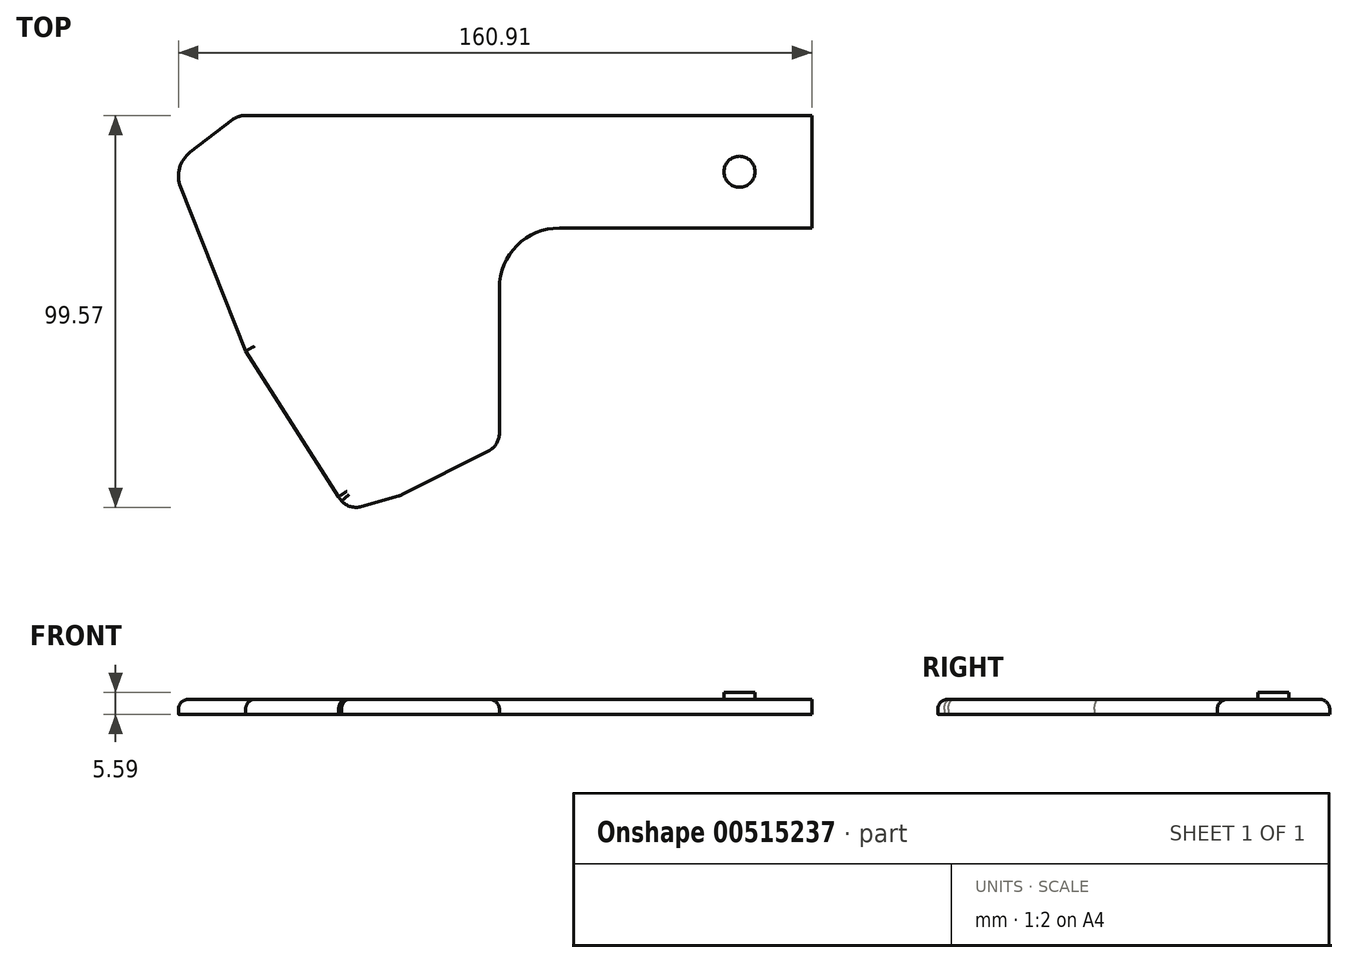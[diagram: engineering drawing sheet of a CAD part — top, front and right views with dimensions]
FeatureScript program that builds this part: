
annotation { "Feature Type Name" : "Feature", "Feature Type Description" : "" }
export const myFeature = defineFeature(function(context is Context, id is Id, definition is map)
    precondition{}
    {
        {
            var Q0;
            Q0=qCreatedBy(makeId("Top.planeOp"),FACE);
            var sketch = newSketch(context, id + "F0", { "sketchPlane" : qUnion([Q0])});
            skLineSegment(sketch, "E0.0", {"start": v(-43.43, -337.67) * mm, "end": v(-15.96, -337.67) * mm});
            skLineSegment(sketch, "E1.0", {"start": v(-160.03, -337.67) * mm, "end": v(-44.7, -337.67) * mm});
            skLineSegment(sketch, "E2.0", {"start": v(-43.43, -309.1) * mm, "end": v(-15.96, -309.1) * mm});
            skLineSegment(sketch, "E3.0", {"start": v(-80.1, -309.1) * mm, "end": v(-44.7, -309.1) * mm});
            skArc(sketch, "E4.0", {"start": v(-80.1, -309.1) * mm, "mid": v(-90.87, -304.63) * mm, "end": v(-95.34, -293.85) * mm});
            skLineSegment(sketch, "E5.0", {"start": v(-95.34, -293.85) * mm, "end": v(-95.34, -256.97) * mm});
            skArc(sketch, "E6.0", {"start": v(-95.34, -256.97) * mm, "mid": v(-96.09, -254.3) * mm, "end": v(-98.12, -252.43) * mm});
            skLineSegment(sketch, "E7.0", {"start": v(-98.12, -252.43) * mm, "end": v(-120.03, -241.33) * mm});
            skArc(sketch, "E8.0", {"start": v(-120.03, -241.33) * mm, "mid": v(-120.47, -241.13) * mm, "end": v(-120.93, -240.97) * mm});
            skLineSegment(sketch, "E9.0", {"start": v(-130.32, -238.3) * mm, "end": v(-120.93, -240.97) * mm});
            skArc(sketch, "E10.0", {"start": v(-130.32, -238.3) * mm, "mid": v(-133.1, -238.29) * mm, "end": v(-135.45, -239.74) * mm});
            skLineSegment(sketch, "E11.0", {"start": v(-136.2, -240.77) * mm, "end": v(-141.2, -248.63) * mm});
            skLineSegment(sketch, "E12.0", {"start": v(-151.3, -264.49) * mm, "end": v(-159.82, -277.9) * mm});
            skLineSegment(sketch, "E13.0", {"start": v(-159.82, -277.9) * mm, "end": v(-165.67, -292.62) * mm});
            skLineSegment(sketch, "E14.0", {"start": v(-172.6, -310.09) * mm, "end": v(-176.33, -319.47) * mm});
            skArc(sketch, "E15.0", {"start": v(-176.33, -319.47) * mm, "mid": v(-176.6, -324.3) * mm, "end": v(-173.9, -328.33) * mm});
            skPoint(sketch, "E16.0", {"position": v(-168.51, -332.47) * mm});
            skLineSegment(sketch, "E17.0", {"start": v(-173.9, -328.33) * mm, "end": v(-163.13, -336.61) * mm});
            skArc(sketch, "E18.0", {"start": v(-163.13, -336.61) * mm, "mid": v(-161.67, -337.4) * mm, "end": v(-160.03, -337.67) * mm});
            skLineSegment(sketch, "E19", {"start": v(-172.6, -310.09) * mm, "end": v(-165.67, -292.62) * mm});
            skLineSegment(sketch, "E20", {"start": v(-151.3, -264.49) * mm, "end": v(-141.2, -248.63) * mm});
            skLineSegment(sketch, "E21", {"start": v(-136.2, -240.77) * mm, "end": v(-135.45, -239.74) * mm});
            skLineSegment(sketch, "E22", {"start": v(-44.7, -309.1) * mm, "end": v(-43.43, -309.1) * mm});
            skLineSegment(sketch, "E23", {"start": v(-44.7, -337.67) * mm, "end": v(-43.43, -337.67) * mm});
            skLineSegment(sketch, "E24", {"start": v(-15.96, -337.67) * mm, "end": v(-15.96, -309.1) * mm});
            skSolve(sketch);
        }
        {
            var Q0;
            Q0=makeQuery(id+"F0.imprint","IMPRINT",FACE,{"disambiguationData":[TD([[makeQuery(id+"F0.imprint","IMPRINT",EDGE,{"derivedFrom":sQuery(id+"F0.wireOp",EDGE,"d1444f51-8acc-4532-b601-094db481933f.0")}),-1.0]])]});
            var Q1;
            Q1=makeQuery(id+"F0.imprint","IMPRINT",FACE,{"disambiguationData":[TD([[makeQuery(id+"F0.imprint","IMPRINT",EDGE,{"derivedFrom":sQuery(id+"F0.wireOp",EDGE,"E0.0")}),1.0]])]});
            var Q2;
            Q2=qConstructionFilter(qBodyType(qCreatedBy(id+"F0",EDGE),BodyType.WIRE),ConstructionObject.NO);
            extrude(context, id + "F1", {"entities" : qUnion([Q0, Q1]), "surfaceEntities" : qUnion([Q2]), "depth" : 3.81 * mm});
        }
        {
            var Q0;
            Q0=makeQuery(id+"F1.opExtrude","CAP_EDGE",EDGE,{"disambiguationData":[OSD([sQuery(id+"F0.wireOp",EDGE,"E21")])],"isStart":false});
            var Q1;
            Q1=makeQuery(id+"F1.opExtrude","CAP_EDGE",EDGE,{"disambiguationData":[OSD([sQuery(id+"F0.wireOp",EDGE,"E9.0")])],"isStart":false});
            var Q2;
            Q2=makeQuery(id+"F1.opExtrude","CAP_EDGE",EDGE,{"disambiguationData":[OSD([sQuery(id+"F0.wireOp",EDGE,"E0.0"),sQuery(id+"F0.wireOp",EDGE,"E1.0"),sQuery(id+"F0.wireOp",EDGE,"E23")])],"isStart":false});
            fillet(context, id + "F2", {"entities" : qUnion([Q0, Q1, Q2]), "radius" : 2.54 * mm, "tangentPropagation" : true, "allowEdgeOverflow" : false});
        }
        {
            var Q0;
            Q0=makeQuery(id+"F1.opExtrude","CAP_FACE",FACE,{"disambiguationData":[OSD([sQuery(id+"F0.wireOp",EDGE,"E0.0"),sQuery(id+"F0.wireOp",EDGE,"E1.0"),sQuery(id+"F0.wireOp",EDGE,"E2.0"),sQuery(id+"F0.wireOp",EDGE,"E3.0"),sQuery(id+"F0.wireOp",EDGE,"E4.0"),sQuery(id+"F0.wireOp",EDGE,"E5.0"),sQuery(id+"F0.wireOp",EDGE,"E6.0"),sQuery(id+"F0.wireOp",EDGE,"E7.0"),sQuery(id+"F0.wireOp",EDGE,"E8.0"),sQuery(id+"F0.wireOp",EDGE,"E9.0"),sQuery(id+"F0.wireOp",EDGE,"E10.0"),sQuery(id+"F0.wireOp",EDGE,"E11.0"),sQuery(id+"F0.wireOp",EDGE,"E12.0"),sQuery(id+"F0.wireOp",EDGE,"E13.0"),sQuery(id+"F0.wireOp",EDGE,"E14.0"),sQuery(id+"F0.wireOp",EDGE,"E15.0"),sQuery(id+"F0.wireOp",EDGE,"E17.0"),sQuery(id+"F0.wireOp",EDGE,"E18.0"),sQuery(id+"F0.wireOp",EDGE,"E19"),sQuery(id+"F0.wireOp",EDGE,"E20"),sQuery(id+"F0.wireOp",EDGE,"E21"),sQuery(id+"F0.wireOp",EDGE,"E22"),sQuery(id+"F0.wireOp",EDGE,"E23"),sQuery(id+"F0.wireOp",EDGE,"E24")])],"isStart":false});
            var sketch = newSketch(context, id + "F3", { "sketchPlane" : qUnion([Q0])});
            skCircle(sketch, "E25.0", {"center": v(-34.35, -323.38) * mm, "radius": 3.94 * mm});
            skLineSegment(sketch, "E26", {"start": v(-97.88, -323.38) * mm, "end": v(-34.35, -323.38) * mm});
            skLineSegment(sketch, "E27", {"start": v(-97.88, -293.85) * mm, "end": v(-97.88, -335.13) * mm});
            skLineSegment(sketch, "E28", {"start": v(-34.35, -323.38) * mm, "end": v(-34.35, -311.63) * mm});
            skLineSegment(sketch, "E29", {"start": v(-34.35, -323.38) * mm, "end": v(-34.35, -335.13) * mm});
            skSolve(sketch);
        }
        {
            var Q0;
            Q0=qSketchRegion(id+"F3",true);
            extrude(context, id + "F4", {"entities" : qUnion([Q0]), "operationType" : NewBodyOperationType.ADD, "depth" : 1.78 * mm});
        }
        {
            var Q0;
            Q0=makeQuery(id+"F1.opExtrude","SWEPT_BODY",BODY,{"disambiguationData":[OSD([sQuery(id+"F0.wireOp",EDGE,"E0.0"),sQuery(id+"F0.wireOp",EDGE,"E1.0"),sQuery(id+"F0.wireOp",EDGE,"E2.0"),sQuery(id+"F0.wireOp",EDGE,"E3.0"),sQuery(id+"F0.wireOp",EDGE,"E4.0"),sQuery(id+"F0.wireOp",EDGE,"E5.0"),sQuery(id+"F0.wireOp",EDGE,"E6.0"),sQuery(id+"F0.wireOp",EDGE,"E7.0"),sQuery(id+"F0.wireOp",EDGE,"E8.0"),sQuery(id+"F0.wireOp",EDGE,"E9.0"),sQuery(id+"F0.wireOp",EDGE,"E10.0"),sQuery(id+"F0.wireOp",EDGE,"E11.0"),sQuery(id+"F0.wireOp",EDGE,"E12.0"),sQuery(id+"F0.wireOp",EDGE,"E13.0"),sQuery(id+"F0.wireOp",EDGE,"E14.0"),sQuery(id+"F0.wireOp",EDGE,"E15.0"),sQuery(id+"F0.wireOp",EDGE,"E17.0"),sQuery(id+"F0.wireOp",EDGE,"E18.0"),sQuery(id+"F0.wireOp",EDGE,"E19"),sQuery(id+"F0.wireOp",EDGE,"E20"),sQuery(id+"F0.wireOp",EDGE,"E21"),sQuery(id+"F0.wireOp",EDGE,"E22"),sQuery(id+"F0.wireOp",EDGE,"E23"),sQuery(id+"F0.wireOp",EDGE,"E24")])]});
            var Q1;
            Q1=qCreatedBy(makeId("Front.planeOp"),FACE);
            mirror(context, id + "F5", {"entities" : qUnion([Q0]), "mirrorPlane" : qUnion([Q1])});
        }
        {
            var Q0;
            Q0=makeQuery(id+"F1.opExtrude","SWEPT_BODY",BODY,{"disambiguationData":[OSD([sQuery(id+"F0.wireOp",EDGE,"E0.0"),sQuery(id+"F0.wireOp",EDGE,"E1.0"),sQuery(id+"F0.wireOp",EDGE,"E2.0"),sQuery(id+"F0.wireOp",EDGE,"E3.0"),sQuery(id+"F0.wireOp",EDGE,"E4.0"),sQuery(id+"F0.wireOp",EDGE,"E5.0"),sQuery(id+"F0.wireOp",EDGE,"E6.0"),sQuery(id+"F0.wireOp",EDGE,"E7.0"),sQuery(id+"F0.wireOp",EDGE,"E8.0"),sQuery(id+"F0.wireOp",EDGE,"E9.0"),sQuery(id+"F0.wireOp",EDGE,"E10.0"),sQuery(id+"F0.wireOp",EDGE,"E11.0"),sQuery(id+"F0.wireOp",EDGE,"E12.0"),sQuery(id+"F0.wireOp",EDGE,"E13.0"),sQuery(id+"F0.wireOp",EDGE,"E14.0"),sQuery(id+"F0.wireOp",EDGE,"E15.0"),sQuery(id+"F0.wireOp",EDGE,"E17.0"),sQuery(id+"F0.wireOp",EDGE,"E18.0"),sQuery(id+"F0.wireOp",EDGE,"E19"),sQuery(id+"F0.wireOp",EDGE,"E20"),sQuery(id+"F0.wireOp",EDGE,"E21"),sQuery(id+"F0.wireOp",EDGE,"E22"),sQuery(id+"F0.wireOp",EDGE,"E23"),sQuery(id+"F0.wireOp",EDGE,"E24")])]});
            deleteBodies(context, id + "F6", {"entities" : qUnion([Q0])});
        }
    });
